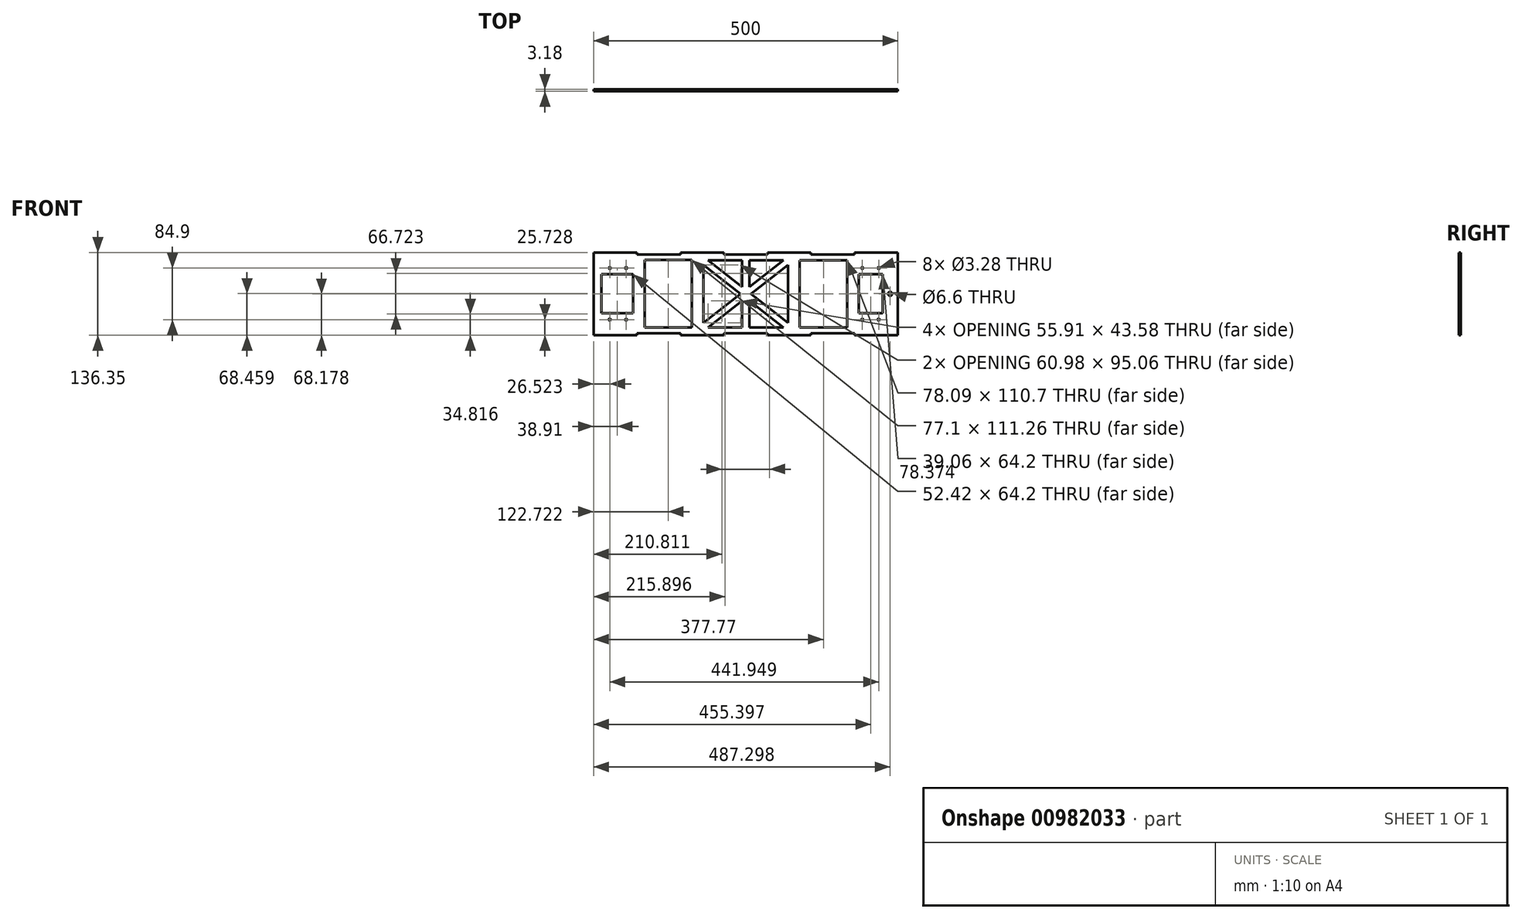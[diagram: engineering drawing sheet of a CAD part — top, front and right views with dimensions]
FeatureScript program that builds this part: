
annotation { "Feature Type Name" : "Feature", "Feature Type Description" : "" }
export const myFeature = defineFeature(function(context is Context, id is Id, definition is map)
    precondition{}
    {
        {
            var Q0;
            Q0=qCreatedBy(makeId("Front.planeOp"),FACE);
            var sketch = newSketch(context, id + "F0", { "sketchPlane" : qUnion([Q0])});
            skLineSegment(sketch, "E0.bottom", {"start": v(162.48, -50.2) * mm, "end": v(-337.52, -50.2) * mm, "construction": true});
            skLineSegment(sketch, "E0.top", {"start": v(162.48, 79.8) * mm, "end": v(-337.52, 79.8) * mm, "construction": true});
            skLineSegment(sketch, "E0.left", {"start": v(162.48, -50.2) * mm, "end": v(162.48, 79.8) * mm});
            skLineSegment(sketch, "E0.right", {"start": v(-337.52, -50.2) * mm, "end": v(-337.52, 79.8) * mm});
            skCircle(sketch, "E1", {"center": v(-297.52, 57.25) * mm, "radius": 4 * mm, "construction": true});
            skLineSegment(sketch, "E2", {"start": v(-297.52, 57.25) * mm, "end": v(-293.52, 57.25) * mm, "construction": true});
            skLineSegment(sketch, "E3", {"start": v(-297.52, 57.25) * mm, "end": v(-297.52, 61.25) * mm, "construction": true});
            skCircle(sketch, "E4", {"center": v(-284.05, 57.25) * mm, "radius": 1.64 * mm});
            skCircle(sketch, "E5.MirrorC", {"center": v(-311, 57.25) * mm, "radius": 1.64 * mm});
            skCircle(sketch, "E6", {"center": v(-297.52, -27.65) * mm, "radius": 4 * mm, "construction": true});
            skLineSegment(sketch, "E7", {"start": v(-297.52, -27.65) * mm, "end": v(-293.52, -27.65) * mm, "construction": true});
            skLineSegment(sketch, "E8", {"start": v(-297.52, -27.65) * mm, "end": v(-297.52, -23.65) * mm, "construction": true});
            skCircle(sketch, "E9", {"center": v(-284.05, -27.65) * mm, "radius": 1.64 * mm});
            skCircle(sketch, "E10.MirrorC", {"center": v(-311, -27.65) * mm, "radius": 1.64 * mm});
            skCircle(sketch, "E11", {"center": v(117.48, -27.65) * mm, "radius": 4 * mm, "construction": true});
            skLineSegment(sketch, "E12", {"start": v(117.48, -27.65) * mm, "end": v(121.48, -27.65) * mm, "construction": true});
            skLineSegment(sketch, "E13", {"start": v(117.48, -27.65) * mm, "end": v(117.48, -23.65) * mm, "construction": true});
            skCircle(sketch, "E14", {"center": v(130.95, -27.65) * mm, "radius": 1.64 * mm});
            skCircle(sketch, "E15.MirrorC", {"center": v(104, -27.65) * mm, "radius": 1.64 * mm});
            skCircle(sketch, "E16", {"center": v(117.48, 57.25) * mm, "radius": 4 * mm, "construction": true});
            skLineSegment(sketch, "E17", {"start": v(117.48, 57.25) * mm, "end": v(121.48, 57.25) * mm, "construction": true});
            skLineSegment(sketch, "E18", {"start": v(117.48, 57.25) * mm, "end": v(117.48, 61.25) * mm, "construction": true});
            skCircle(sketch, "E19", {"center": v(130.95, 57.25) * mm, "radius": 1.64 * mm});
            skCircle(sketch, "E20.MirrorC", {"center": v(104, 57.25) * mm, "radius": 1.64 * mm});
            skPoint(sketch, "E21.middle.positionSnap0", {"position": v(-297.52, -25.65) * mm});
            skPoint(sketch, "E21.centerSnap0", {"position": v(-297.52, -25.65) * mm});
            skCircle(sketch, "E22", {"center": v(149.78, 14.8) * mm, "radius": 3.3 * mm});
            skLineSegment(sketch, "E23", {"start": v(-87.52, 79.8) * mm, "end": v(-87.52, -50.2) * mm, "construction": true});
            skLineSegment(sketch, "E24", {"start": v(-87.52, 14.8) * mm, "end": v(-337.52, 14.8) * mm, "construction": true});
            skLineSegment(sketch, "E25.right", {"start": v(-324.82, -17.3) * mm, "end": v(-324.82, 46.9) * mm});
            skPoint(sketch, "E25.middle", {"position": v(-246.56, 14.8) * mm});
            skLineSegment(sketch, "E26", {"start": v(-87.52, 14.8) * mm, "end": v(162.48, 14.8) * mm, "construction": true});
            skLineSegment(sketch, "E27.right", {"start": v(137.4, 47.18) * mm, "end": v(137.4, -17.02) * mm});
            skLineSegment(sketch, "E28", {"start": v(1.2, 70.15) * mm, "end": v(1.2, -40.55) * mm});
            skLineSegment(sketch, "E29", {"start": v(-176.25, 70.43) * mm, "end": v(-176.25, -40.83) * mm});
            skLineSegment(sketch, "E30.right", {"start": v(-272.4, 46.9) * mm, "end": v(-272.4, -17.3) * mm});
            skLineSegment(sketch, "E31", {"start": v(-324.82, 46.9) * mm, "end": v(-272.4, 46.9) * mm});
            skLineSegment(sketch, "E32", {"start": v(-324.82, -17.3) * mm, "end": v(-272.4, -17.3) * mm});
            skLineSegment(sketch, "E33.right", {"start": v(98.35, 47.18) * mm, "end": v(98.35, -17.02) * mm});
            skLineSegment(sketch, "E34", {"start": v(98.35, 47.18) * mm, "end": v(137.4, 47.18) * mm});
            skLineSegment(sketch, "E35", {"start": v(98.35, -17.02) * mm, "end": v(137.4, -17.02) * mm});
            skLineSegment(sketch, "E36.bottom", {"start": v(-17.85, -40.35) * mm, "end": v(-157.2, -40.35) * mm});
            skLineSegment(sketch, "E36.top", {"start": v(-17.85, 69.95) * mm, "end": v(-157.2, 69.95) * mm});
            skLineSegment(sketch, "E36.left", {"start": v(-17.85, -40.35) * mm, "end": v(-17.85, 69.95) * mm});
            skLineSegment(sketch, "E36.right", {"start": v(-157.2, -40.35) * mm, "end": v(-157.2, 69.95) * mm});
            skPoint(sketch, "E36.middle", {"position": v(-87.52, 14.8) * mm});
            skLineSegment(sketch, "E37", {"start": v(-157.2, 62.33) * mm, "end": v(-25.47, -40.35) * mm});
            skLineSegment(sketch, "E38", {"start": v(-149.58, 69.95) * mm, "end": v(-17.85, -32.73) * mm});
            skLineSegment(sketch, "E39.MirrorCS", {"start": v(-25.47, 69.95) * mm, "end": v(-157.2, -32.73) * mm});
            skLineSegment(sketch, "E40.MirrorCS", {"start": v(-17.85, 62.33) * mm, "end": v(-149.58, -40.35) * mm});
            skLineSegment(sketch, "E41.bottom", {"start": v(-81.38, -40.35) * mm, "end": v(-93.67, -40.35) * mm});
            skLineSegment(sketch, "E41.top", {"start": v(-81.38, 69.95) * mm, "end": v(-93.67, 69.95) * mm});
            skLineSegment(sketch, "E41.left", {"start": v(-81.38, -40.35) * mm, "end": v(-81.38, 69.95) * mm});
            skLineSegment(sketch, "E41.right", {"start": v(-93.67, -40.35) * mm, "end": v(-93.67, 69.95) * mm});
            skLineSegment(sketch, "E42", {"start": v(-253.35, 70.43) * mm, "end": v(-253.35, -40.83) * mm});
            skLineSegment(sketch, "E43", {"start": v(-253.35, 70.43) * mm, "end": v(-176.25, 70.43) * mm});
            skLineSegment(sketch, "E44", {"start": v(-253.35, -40.83) * mm, "end": v(-176.25, -40.83) * mm});
            skLineSegment(sketch, "E45", {"start": v(79.3, 70.15) * mm, "end": v(79.3, -40.55) * mm});
            skLineSegment(sketch, "E46", {"start": v(1.2, 70.15) * mm, "end": v(79.3, 70.15) * mm});
            skLineSegment(sketch, "E47", {"start": v(1.2, -40.55) * mm, "end": v(79.3, -40.55) * mm});
            skLineSegment(sketch, "E48.top", {"start": v(-337.52, -53.38) * mm, "end": v(-266.1, -53.38) * mm});
            skLineSegment(sketch, "E48.left", {"start": v(-337.52, -50.2) * mm, "end": v(-337.52, -53.38) * mm});
            skLineSegment(sketch, "E48.right", {"start": v(-266.1, -50.2) * mm, "end": v(-266.1, -53.38) * mm});
            skLineSegment(sketch, "E49.bottom", {"start": v(-266.1, -50.2) * mm, "end": v(-194.66, -50.2) * mm});
            skLineSegment(sketch, "E50.1.0.0", {"start": v(-194.66, -53.38) * mm, "end": v(-123.24, -53.38) * mm});
            skLineSegment(sketch, "E50.1.0.1", {"start": v(-123.24, -50.2) * mm, "end": v(-51.8, -50.2) * mm});
            skLineSegment(sketch, "E50.1.0.2", {"start": v(-194.66, -50.2) * mm, "end": v(-194.66, -53.38) * mm});
            skLineSegment(sketch, "E50.1.0.3", {"start": v(-123.24, -50.2) * mm, "end": v(-123.24, -53.38) * mm});
            skLineSegment(sketch, "E50.1.0.4", {"start": v(-123.24, -50.2) * mm, "end": v(-123.24, -53.38) * mm});
            skLineSegment(sketch, "E50.2.0.0", {"start": v(-51.8, -53.38) * mm, "end": v(19.62, -53.38) * mm});
            skLineSegment(sketch, "E50.2.0.1", {"start": v(19.62, -50.2) * mm, "end": v(91.05, -50.2) * mm});
            skLineSegment(sketch, "E50.2.0.2", {"start": v(-51.8, -50.2) * mm, "end": v(-51.8, -53.38) * mm});
            skLineSegment(sketch, "E50.2.0.3", {"start": v(19.62, -50.2) * mm, "end": v(19.62, -53.38) * mm});
            skLineSegment(sketch, "E50.2.0.4", {"start": v(19.62, -50.2) * mm, "end": v(19.62, -53.38) * mm});
            skLineSegment(sketch, "E50.3.0.0", {"start": v(91.05, -53.38) * mm, "end": v(162.48, -53.38) * mm});
            skLineSegment(sketch, "E50.3.0.2", {"start": v(91.05, -50.2) * mm, "end": v(91.05, -53.38) * mm});
            skLineSegment(sketch, "E50.3.0.3", {"start": v(162.48, -50.2) * mm, "end": v(162.48, -53.38) * mm});
            skLineSegment(sketch, "E50.3.0.4", {"start": v(162.48, -50.2) * mm, "end": v(162.48, -53.38) * mm});
            skLineSegment(sketch, "E50.direction1", {"start": v(-337.52, -53.38) * mm, "end": v(-194.66, -53.38) * mm, "construction": true});
            skLineSegment(sketch, "E51.MirrorCS", {"start": v(162.48, 79.8) * mm, "end": v(162.48, 82.97) * mm});
            skLineSegment(sketch, "E52.MirrorCS", {"start": v(-123.24, 79.8) * mm, "end": v(-123.24, 82.97) * mm});
            skLineSegment(sketch, "E53.MirrorCS", {"start": v(-266.1, 79.8) * mm, "end": v(-266.1, 82.97) * mm});
            skLineSegment(sketch, "E54.MirrorCS", {"start": v(19.62, 79.8) * mm, "end": v(19.62, 82.97) * mm});
            skLineSegment(sketch, "E55.MirrorCS", {"start": v(-194.66, 79.8) * mm, "end": v(-194.66, 82.97) * mm});
            skLineSegment(sketch, "E56.MirrorCS", {"start": v(-337.52, 79.8) * mm, "end": v(-337.52, 82.97) * mm});
            skLineSegment(sketch, "E57.MirrorCS", {"start": v(-51.8, 79.8) * mm, "end": v(-51.8, 82.97) * mm});
            skLineSegment(sketch, "E58.MirrorCS", {"start": v(91.05, 79.8) * mm, "end": v(91.05, 82.97) * mm});
            skLineSegment(sketch, "E59.MirrorCS", {"start": v(-123.24, 79.8) * mm, "end": v(-51.8, 79.8) * mm});
            skLineSegment(sketch, "E60.MirrorCS", {"start": v(19.62, 79.8) * mm, "end": v(91.05, 79.8) * mm});
            skLineSegment(sketch, "E61.MirrorCS", {"start": v(-337.52, 82.97) * mm, "end": v(-266.1, 82.97) * mm});
            skLineSegment(sketch, "E62.MirrorCS", {"start": v(-266.1, 79.8) * mm, "end": v(-194.66, 79.8) * mm});
            skLineSegment(sketch, "E63.MirrorCS", {"start": v(-51.8, 82.97) * mm, "end": v(19.62, 82.97) * mm});
            skLineSegment(sketch, "E64.MirrorCS", {"start": v(-337.52, 82.97) * mm, "end": v(-194.66, 82.97) * mm, "construction": true});
            skLineSegment(sketch, "E65.MirrorCS", {"start": v(-194.66, 82.97) * mm, "end": v(-123.24, 82.97) * mm});
            skLineSegment(sketch, "E66.MirrorCS", {"start": v(91.05, 82.97) * mm, "end": v(162.48, 82.97) * mm});
            skSolve(sketch);
        }
        {
            var Q0;
            Q0=makeQuery(id+"F0.imprint","IMPRINT",FACE,{"disambiguationData":[TD([[makeQuery(id+"F0.imprint","IMPRINT",EDGE,{"derivedFrom":sQuery(id+"F0.wireOp",EDGE,"E0.left")}),1.0]])]});
            var Q1;
            {var subQ1=sQuery(id+"F0.wireOp",EDGE,"E36.top");var subQ6=sQuery(id+"F0.wireOp",EDGE,"E36.right");var subQ10=makeQuery(id+"F0.imprint","INTERSECT",VERTEX,{"derivedFrom":[subQ1,subQ6]});Q1=makeQuery(id+"F0.imprint","IMPRINT",FACE,{"disambiguationData":[TD([[makeQuery(id+"F0.imprint","IMPRINT",EDGE,{"disambiguationData":[TD([[subQ10,1.0]])],"derivedFrom":subQ1}),1.0]])]});}
            var Q2;
            {var subQ6=sQuery(id+"F0.wireOp",EDGE,"E36.top");var subQ9=sQuery(id+"F0.wireOp",EDGE,"E36.left");var subQ10=makeQuery(id+"F0.imprint","INTERSECT",VERTEX,{"derivedFrom":[subQ6,subQ9]});Q2=makeQuery(id+"F0.imprint","IMPRINT",FACE,{"disambiguationData":[TD([[makeQuery(id+"F0.imprint","IMPRINT",EDGE,{"disambiguationData":[TD([[subQ10,-1.0]])],"derivedFrom":subQ6}),1.0]])]});}
            var Q3;
            {var subQ0=sQuery(id+"F0.wireOp",EDGE,"E37");var subQ1=sQuery(id+"F0.wireOp",EDGE,"E36.bottom");var subQ2=makeQuery(id+"F0.imprint","INTERSECT",VERTEX,{"derivedFrom":[subQ1,subQ0]});Q3=makeQuery(id+"F0.imprint","IMPRINT",FACE,{"disambiguationData":[TD([[makeQuery(id+"F0.imprint","IMPRINT",EDGE,{"disambiguationData":[TD([[subQ2,1.0]])],"derivedFrom":subQ1}),-1.0]])]});}
            var Q4;
            {var subQ1=sQuery(id+"F0.wireOp",EDGE,"E36.right");var subQ7=sQuery(id+"F0.wireOp",EDGE,"E36.bottom");var subQ8=makeQuery(id+"F0.imprint","INTERSECT",VERTEX,{"derivedFrom":[subQ7,subQ1]});Q4=makeQuery(id+"F0.imprint","IMPRINT",FACE,{"disambiguationData":[TD([[makeQuery(id+"F0.imprint","IMPRINT",EDGE,{"disambiguationData":[TD([[subQ8,1.0]])],"derivedFrom":subQ7}),-1.0]])]});}
            var Q5;
            {var subQ1=sQuery(id+"F0.wireOp",EDGE,"E36.bottom");var subQ7=sQuery(id+"F0.wireOp",EDGE,"E41.right");var subQ9=makeQuery(id+"F0.imprint","INTERSECT",VERTEX,{"derivedFrom":[subQ1,subQ7]});Q5=makeQuery(id+"F0.imprint","IMPRINT",FACE,{"disambiguationData":[TD([[makeQuery(id+"F0.imprint","IMPRINT",EDGE,{"disambiguationData":[TD([[subQ9,1.0]])],"derivedFrom":subQ1}),-1.0]])]});}
            var Q6;
            {var subQ0=sQuery(id+"F0.wireOp",EDGE,"E41.left");var subQ1=sQuery(id+"F0.wireOp",EDGE,"E37");var subQ2=makeQuery(id+"F0.imprint","INTERSECT",VERTEX,{"derivedFrom":[subQ1,subQ0]});Q6=makeQuery(id+"F0.imprint","IMPRINT",FACE,{"disambiguationData":[TD([[makeQuery(id+"F0.imprint","IMPRINT",EDGE,{"disambiguationData":[TD([[subQ2,1.0]])],"derivedFrom":subQ1}),1.0]])]});}
            var Q7;
            {var subQ0=sQuery(id+"F0.wireOp",EDGE,"E41.right");var subQ1=sQuery(id+"F0.wireOp",EDGE,"E37");var subQ2=makeQuery(id+"F0.imprint","INTERSECT",VERTEX,{"derivedFrom":[subQ1,subQ0]});Q7=makeQuery(id+"F0.imprint","IMPRINT",FACE,{"disambiguationData":[TD([[makeQuery(id+"F0.imprint","IMPRINT",EDGE,{"disambiguationData":[TD([[subQ2,-1.0]])],"derivedFrom":subQ1}),-1.0]])]});}
            var Q8;
            {var subQ0=sQuery(id+"F0.wireOp",EDGE,"E41.right");var subQ1=sQuery(id+"F0.wireOp",EDGE,"E37");var subQ2=makeQuery(id+"F0.imprint","INTERSECT",VERTEX,{"derivedFrom":[subQ1,subQ0]});Q8=makeQuery(id+"F0.imprint","IMPRINT",FACE,{"disambiguationData":[TD([[makeQuery(id+"F0.imprint","IMPRINT",EDGE,{"disambiguationData":[TD([[subQ2,1.0]])],"derivedFrom":subQ1}),1.0]])]});}
            var Q9;
            {var subQ3=sQuery(id+"F0.wireOp",EDGE,"E37");var subQ9=sQuery(id+"F0.wireOp",EDGE,"E41.right");var subQ10=makeQuery(id+"F0.imprint","INTERSECT",VERTEX,{"derivedFrom":[subQ3,subQ9]});Q9=makeQuery(id+"F0.imprint","IMPRINT",FACE,{"disambiguationData":[TD([[makeQuery(id+"F0.imprint","IMPRINT",EDGE,{"disambiguationData":[TD([[subQ10,-1.0]])],"derivedFrom":subQ3}),1.0]])]});}
            var Q10;
            {var subQ0=sQuery(id+"F0.wireOp",EDGE,"E41.left");var subQ1=sQuery(id+"F0.wireOp",EDGE,"E38");var subQ2=makeQuery(id+"F0.imprint","INTERSECT",VERTEX,{"derivedFrom":[subQ1,subQ0]});Q10=makeQuery(id+"F0.imprint","IMPRINT",FACE,{"disambiguationData":[TD([[makeQuery(id+"F0.imprint","IMPRINT",EDGE,{"disambiguationData":[TD([[subQ2,1.0]])],"derivedFrom":subQ1}),1.0]])]});}
            var Q11;
            {var subQ0=sQuery(id+"F0.wireOp",EDGE,"E41.right");var subQ1=sQuery(id+"F0.wireOp",EDGE,"E38");var subQ2=makeQuery(id+"F0.imprint","INTERSECT",VERTEX,{"derivedFrom":[subQ1,subQ0]});Q11=makeQuery(id+"F0.imprint","IMPRINT",FACE,{"disambiguationData":[TD([[makeQuery(id+"F0.imprint","IMPRINT",EDGE,{"disambiguationData":[TD([[subQ2,-1.0]])],"derivedFrom":subQ1}),-1.0]])]});}
            var Q12;
            {var subQ5=sQuery(id+"F0.wireOp",EDGE,"E41.right");var subQ7=sQuery(id+"F0.wireOp",EDGE,"E36.top");var subQ9=makeQuery(id+"F0.imprint","INTERSECT",VERTEX,{"derivedFrom":[subQ7,subQ5]});Q12=makeQuery(id+"F0.imprint","IMPRINT",FACE,{"disambiguationData":[TD([[makeQuery(id+"F0.imprint","IMPRINT",EDGE,{"disambiguationData":[TD([[subQ9,1.0]])],"derivedFrom":subQ7}),1.0]])]});}
            var Q13;
            {var subQ0=sQuery(id+"F0.wireOp",EDGE,"E40.MirrorCS");var subQ1=sQuery(id+"F0.wireOp",EDGE,"E38");var subQ2=makeQuery(id+"F0.imprint","INTERSECT",VERTEX,{"derivedFrom":[subQ1,subQ0]});Q13=makeQuery(id+"F0.imprint","IMPRINT",FACE,{"disambiguationData":[TD([[makeQuery(id+"F0.imprint","IMPRINT",EDGE,{"disambiguationData":[TD([[subQ2,1.0]])],"derivedFrom":subQ1}),-1.0]])]});}
            extrude(context, id + "F1", {"entities" : qUnion([Q0, Q1, Q2, Q3, Q4, Q5, Q6, Q7, Q8, Q9, Q10, Q11, Q12, Q13]), "depth" : 3.17 * mm, "offsetDistance" : 25.4 * mm});
        }
    });
